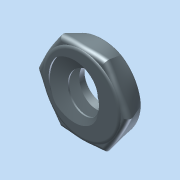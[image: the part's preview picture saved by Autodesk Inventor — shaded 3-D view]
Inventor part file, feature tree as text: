
AUTODESK INVENTOR PART (.ipt)
format: ipt  version: 2015 (Build 190159000, 159)  size: 637,440 bytes
history: native  units: in
note: dims shown in document units (in); Inventor stores cm internally (conversion verified against a paired STEP export)
features: other x2, plane x2, sketch x2, imported_body x1
ambient origin geometry x8: Origin, YZ Plane, XZ Plane, XY Plane, X Axis, Y Axis, Z Axis, Center Point
bodies: Body1 (feature_tree)
feature tree (7):
  other  "Baseplate Nut"
  other  "Baseplate Nut.ipt1"
  plane  "Work Plane1"
  plane  "Work Plane2"
  sketch  "3D Sketch1"
  sketch  "3D Sketch2"
  imported_body  "Base1"
